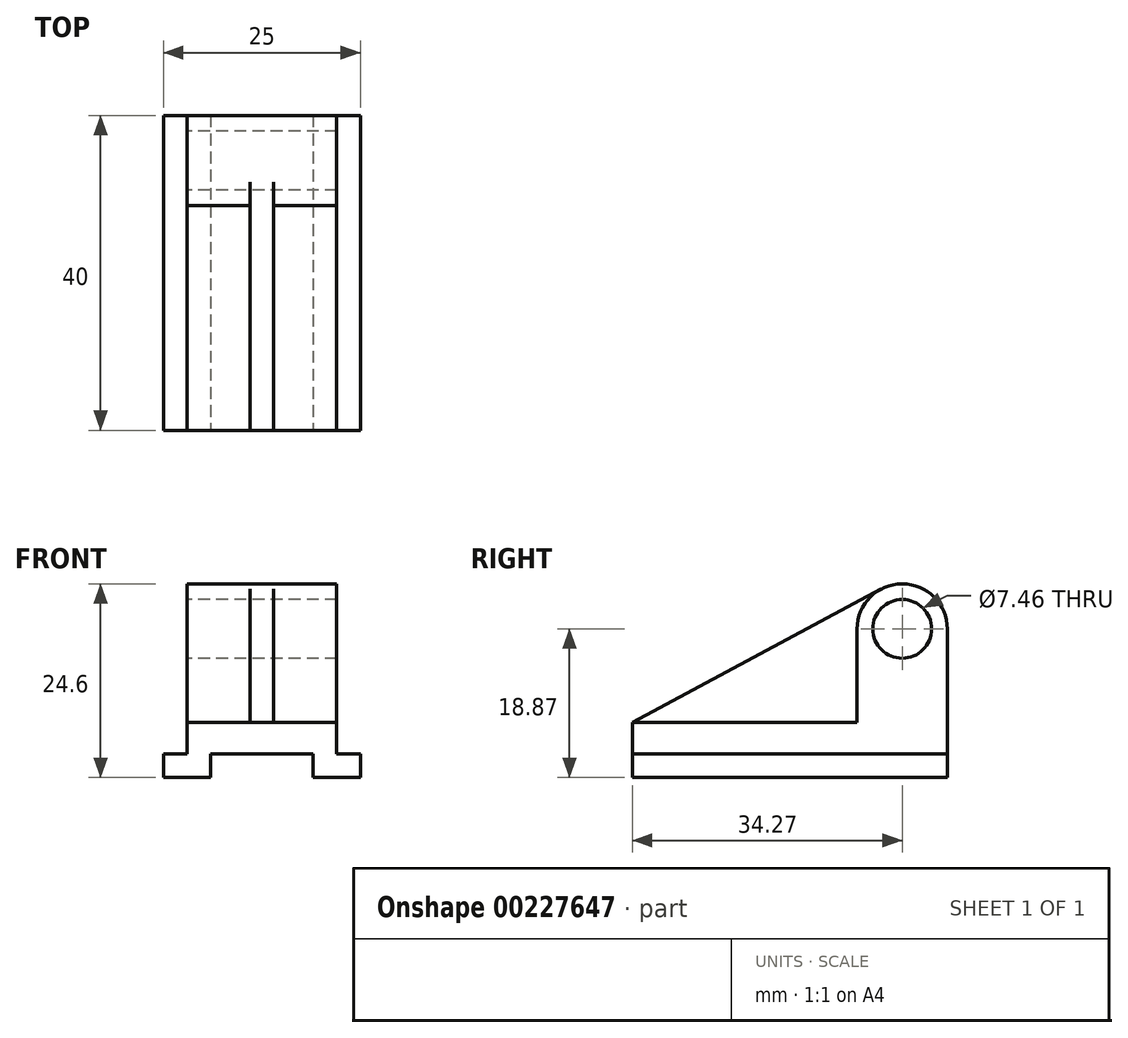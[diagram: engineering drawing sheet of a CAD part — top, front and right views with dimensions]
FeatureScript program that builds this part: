
annotation { "Feature Type Name" : "Feature", "Feature Type Description" : "" }
export const myFeature = defineFeature(function(context is Context, id is Id, definition is map)
    precondition{}
    {
        {
            var Q0;
            Q0=qCreatedBy(makeId("Right.planeOp"),FACE);
            var sketch = newSketch(context, id + "F0", { "sketchPlane" : qUnion([Q0])});
            skLineSegment(sketch, "E0", {"start": v(0, 0) * mm, "end": v(40, 0) * mm});
            skLineSegment(sketch, "E1", {"start": v(40, 0) * mm, "end": v(40, 3) * mm});
            skLineSegment(sketch, "E2", {"start": v(40, 3) * mm, "end": v(0, 3) * mm});
            skLineSegment(sketch, "E3", {"start": v(0, 3) * mm, "end": v(0, 0) * mm});
            skLineSegment(sketch, "E4", {"start": v(0, 3) * mm, "end": v(0, 7) * mm});
            skLineSegment(sketch, "E5", {"start": v(0, 7) * mm, "end": v(28.54, 7) * mm});
            skArc(sketch, "E6", {"start": v(40, 18.87) * mm, "mid": v(34.27, 24.6) * mm, "end": v(28.54, 18.87) * mm});
            skCircle(sketch, "E7", {"center": v(34.27, 18.87) * mm, "radius": 3.73 * mm});
            skLineSegment(sketch, "E8", {"start": v(40, 3) * mm, "end": v(40, 18.87) * mm});
            skLineSegment(sketch, "E9", {"start": v(28.54, 18.87) * mm, "end": v(28.54, 7) * mm});
            skLineSegment(sketch, "E10", {"start": v(28.54, 7) * mm, "end": v(40, 7) * mm});
            skLineSegment(sketch, "E11", {"start": v(0, 7) * mm, "end": v(31.56, 23.92) * mm});
            skSolve(sketch);
        }
        {
            var Q0;
            Q0=makeQuery(id+"F0.imprint","IMPRINT",FACE,{"disambiguationData":[TD([[makeQuery(id+"F0.imprint","IMPRINT",EDGE,{"derivedFrom":sQuery(id+"F0.wireOp",EDGE,"E0")}),1.0]])]});
            extrude(context, id + "F1", {"entities" : qUnion([Q0]), "endBound" : BoundingType.SYMMETRIC, "depth" : 25 * mm});
        }
        {
            var Q0;
            {var subQ1=sQuery(id+"F0.wireOp",EDGE,"E2");Q0=makeQuery(id+"F0.imprint","IMPRINT",FACE,{"disambiguationData":[TD([[makeQuery(id+"F0.imprint","IMPRINT",EDGE,{"derivedFrom":subQ1}),-1.0]])]});}
            extrude(context, id + "F2", {"entities" : qUnion([Q0]), "operationType" : NewBodyOperationType.ADD, "endBound" : BoundingType.SYMMETRIC, "depth" : 19 * mm});
        }
        {
            var Q0;
            {var subQ1=sQuery(id+"F0.wireOp",EDGE,"E6");Q0=makeQuery(id+"F0.imprint","IMPRINT",FACE,{"disambiguationData":[TD([[makeQuery(id+"F0.imprint","IMPRINT",EDGE,{"derivedFrom":subQ1}),1.0]])]});}
            extrude(context, id + "F3", {"entities" : qUnion([Q0]), "operationType" : NewBodyOperationType.ADD, "endBound" : BoundingType.SYMMETRIC, "depth" : 19 * mm});
        }
        {
            var Q0;
            Q0=makeQuery(id+"F0.imprint","IMPRINT",FACE,{"disambiguationData":[TD([[makeQuery(id+"F0.imprint","IMPRINT",EDGE,{"derivedFrom":sQuery(id+"F0.wireOp",EDGE,"E5")}),1.0]])]});
            extrude(context, id + "F4", {"entities" : qUnion([Q0]), "operationType" : NewBodyOperationType.ADD, "endBound" : BoundingType.SYMMETRIC, "depth" : 3 * mm});
        }
        {
            var Q0;
            Q0=makeQuery(id+"F2.boolean.opBoolean","MERGE",FACE,{"derivedFrom":[makeQuery(id+"F1.opExtrude","SWEPT_FACE",FACE,{"disambiguationData":[OSD([sQuery(id+"F0.wireOp",EDGE,"E3")])]}),makeQuery(id+"F2.opExtrude","SWEPT_FACE",FACE,{"disambiguationData":[OSD([sQuery(id+"F0.wireOp",EDGE,"E4")])]})]});
            var sketch = newSketch(context, id + "F5", { "sketchPlane" : qUnion([Q0])});
            skLineSegment(sketch, "E12.bottom", {"start": v(-6.5, 3) * mm, "end": v(6.5, 3) * mm});
            skLineSegment(sketch, "E12.left", {"start": v(-6.5, 3) * mm, "end": v(-6.5, 0) * mm});
            skLineSegment(sketch, "E12.right", {"start": v(6.5, 3) * mm, "end": v(6.5, 0) * mm});
            skLineSegment(sketch, "E13", {"start": v(-6.5, 0) * mm, "end": v(6.5, 0) * mm});
            skSolve(sketch);
        }
        {
            var Q0;
            Q0=makeQuery(id+"F5.imprint","IMPRINT",FACE,{"disambiguationData":[TD([[makeQuery(id+"F5.imprint","IMPRINT",EDGE,{"derivedFrom":sQuery(id+"F5.wireOp",EDGE,"E12.bottom")}),-1.0]])]});
            extrude(context, id + "F6", {"entities" : qUnion([Q0]), "operationType" : NewBodyOperationType.REMOVE, "endBound" : BoundingType.UP_TO_NEXT, "oppositeDirection" : true, "depth" : 25 * mm});
        }
    });
